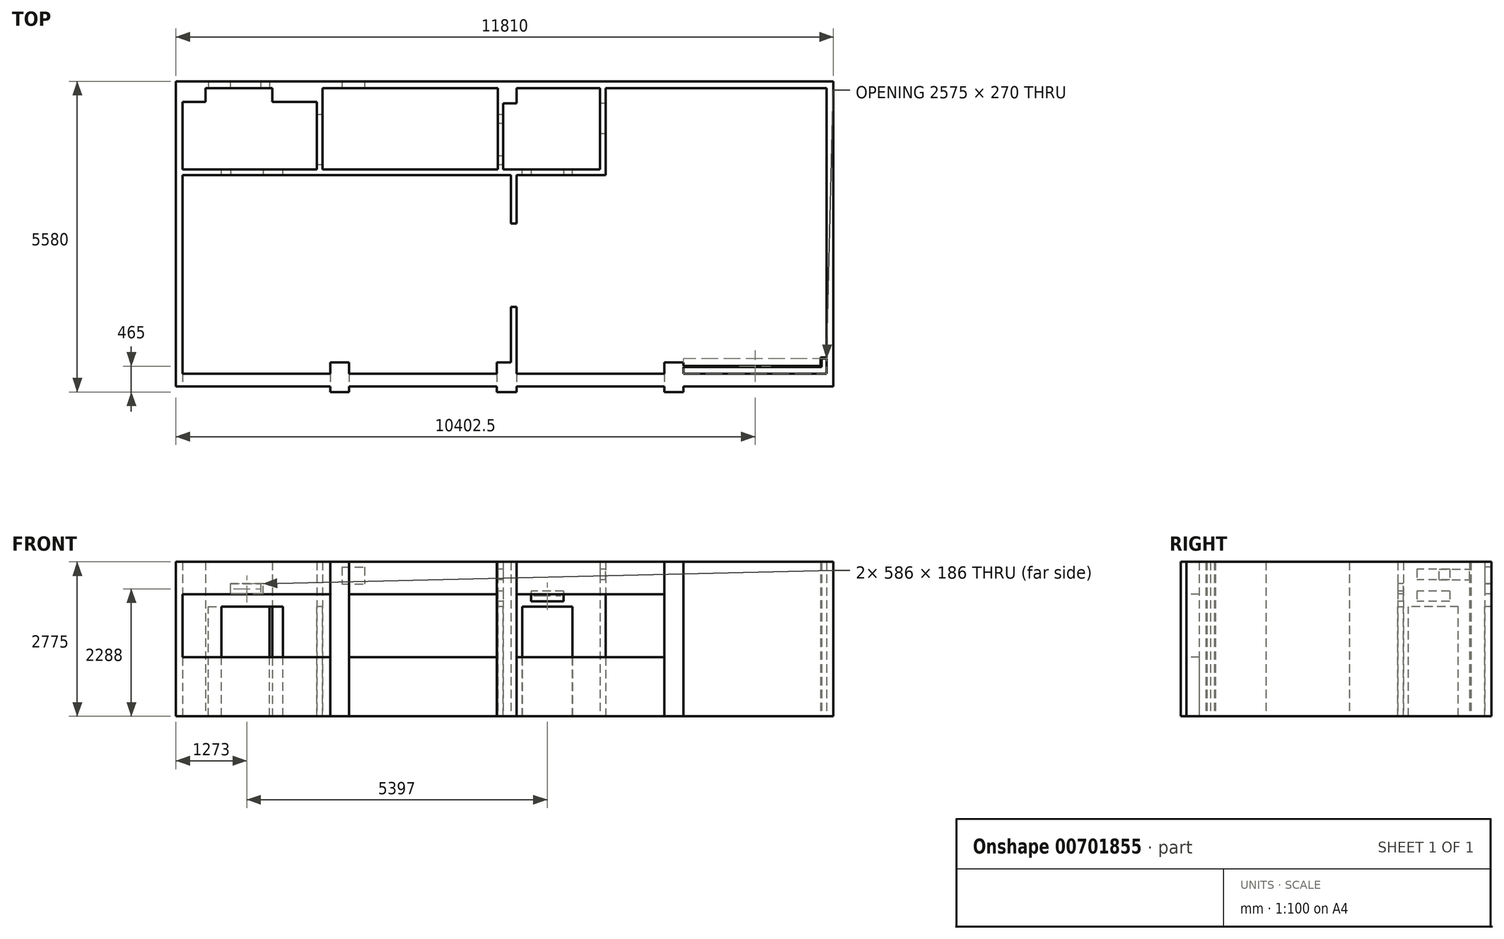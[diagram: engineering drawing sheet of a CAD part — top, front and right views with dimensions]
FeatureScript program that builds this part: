
annotation { "Feature Type Name" : "Feature", "Feature Type Description" : "" }
export const myFeature = defineFeature(function(context is Context, id is Id, definition is map)
    precondition{}
    {
        {
            var Q0;
            Q0=qCreatedBy(makeId("Top.planeOp"),FACE);
            var sketch = newSketch(context, id + "F0", { "sketchPlane" : qUnion([Q0])});
            skLineSegment(sketch, "E0.bottom", {"start": v(0, 0) * mm, "end": v(-5570, 0) * mm});
            skLineSegment(sketch, "E0.top", {"start": v(0, -5240) * mm, "end": v(-2575, -5240) * mm, "construction": true});
            skLineSegment(sketch, "E0.left", {"start": v(0, 0) * mm, "end": v(0, -5240) * mm});
            skLineSegment(sketch, "E0.right", {"start": v(-11570, -250) * mm, "end": v(-11570, -5130) * mm});
            skLineSegment(sketch, "E1.bottom", {"start": v(-11690, 120) * mm, "end": v(120, 120) * mm});
            skLineSegment(sketch, "E1.top", {"start": v(-11690, -5360) * mm, "end": v(-8920, -5360) * mm});
            skLineSegment(sketch, "E1.left", {"start": v(-11690, 120) * mm, "end": v(-11690, -5360) * mm});
            skLineSegment(sketch, "E1.right", {"start": v(120, 120) * mm, "end": v(120, -5360) * mm});
            skLineSegment(sketch, "E2.trimOffspring", {"start": v(-5925, -5240) * mm, "end": v(-8580, -5240) * mm, "construction": true});
            skLineSegment(sketch, "E3.trimOffspring", {"start": v(-5910, 0) * mm, "end": v(-9070, 0) * mm});
            skLineSegment(sketch, "E4", {"start": v(-5910, 0) * mm, "end": v(-5910, -275) * mm});
            skLineSegment(sketch, "E5", {"start": v(-5910, -275) * mm, "end": v(-5570, -275) * mm});
            skLineSegment(sketch, "E6", {"start": v(-5570, -275) * mm, "end": v(-5570, 0) * mm});
            skLineSegment(sketch, "E7", {"start": v(-5925, -5130) * mm, "end": v(-5925, -4930) * mm});
            skLineSegment(sketch, "E8", {"start": v(-5925, -4930) * mm, "end": v(-5570, -4930) * mm});
            skLineSegment(sketch, "E9", {"start": v(-5570, -4930) * mm, "end": v(-5570, -5130) * mm});
            skLineSegment(sketch, "E10.top", {"start": v(-8580, -4930) * mm, "end": v(-8920, -4930) * mm});
            skLineSegment(sketch, "E10.left", {"start": v(-8580, -5130) * mm, "end": v(-8580, -4930) * mm});
            skLineSegment(sketch, "E10.right", {"start": v(-8920, -5130) * mm, "end": v(-8920, -4930) * mm});
            skLineSegment(sketch, "E11.trimOffspring", {"start": v(-8920, -5240) * mm, "end": v(-11570, -5240) * mm, "construction": true});
            skLineSegment(sketch, "E12.top", {"start": v(-11570, -250) * mm, "end": v(-11160, -250) * mm});
            skLineSegment(sketch, "E12.right", {"start": v(-11160, 0) * mm, "end": v(-11160, -250) * mm});
            skLineSegment(sketch, "E13.top", {"start": v(-9960, -250) * mm, "end": v(-9070, -250) * mm});
            skLineSegment(sketch, "E13.left", {"start": v(-9960, 0) * mm, "end": v(-9960, -250) * mm});
            skLineSegment(sketch, "E13.right", {"start": v(-9070, 0) * mm, "end": v(-9070, -250) * mm});
            skLineSegment(sketch, "E14.trimOffspring", {"start": v(-9960, 0) * mm, "end": v(-11160, 0) * mm});
            skLineSegment(sketch, "E15.top", {"start": v(-2915, -4930) * mm, "end": v(-2575, -4930) * mm});
            skLineSegment(sketch, "E15.left", {"start": v(-2915, -5130) * mm, "end": v(-2915, -4930) * mm});
            skLineSegment(sketch, "E15.right", {"start": v(-2575, -5130) * mm, "end": v(-2575, -4930) * mm});
            skLineSegment(sketch, "E16.top", {"start": v(-2575, -5460) * mm, "end": v(-2915, -5460) * mm});
            skLineSegment(sketch, "E16.left", {"start": v(-2575, -5360) * mm, "end": v(-2575, -5460) * mm});
            skLineSegment(sketch, "E16.right", {"start": v(-2915, -5360) * mm, "end": v(-2915, -5460) * mm});
            skLineSegment(sketch, "E17.trimOffspring", {"start": v(-2575, -5360) * mm, "end": v(120, -5360) * mm});
            skLineSegment(sketch, "E18.trimOffspring", {"start": v(-2915, -5240) * mm, "end": v(-5570, -5240) * mm, "construction": true});
            skLineSegment(sketch, "E19.top", {"start": v(-5570, -5460) * mm, "end": v(-5925, -5460) * mm});
            skLineSegment(sketch, "E19.left", {"start": v(-5570, -5360) * mm, "end": v(-5570, -5460) * mm});
            skLineSegment(sketch, "E19.right", {"start": v(-5925, -5360) * mm, "end": v(-5925, -5460) * mm});
            skLineSegment(sketch, "E20.top", {"start": v(-8580, -5460) * mm, "end": v(-8920, -5460) * mm});
            skLineSegment(sketch, "E20.left", {"start": v(-8580, -5360) * mm, "end": v(-8580, -5460) * mm});
            skLineSegment(sketch, "E20.right", {"start": v(-8920, -5360) * mm, "end": v(-8920, -5460) * mm});
            skLineSegment(sketch, "E21.trimOffspring", {"start": v(-8580, -5360) * mm, "end": v(-5925, -5360) * mm});
            skLineSegment(sketch, "E22.trimOffspring", {"start": v(-5570, -5360) * mm, "end": v(-2915, -5360) * mm});
            skLineSegment(sketch, "E23", {"start": v(-11570, -5130) * mm, "end": v(-8920, -5130) * mm});
            skLineSegment(sketch, "E24.trimOffspring", {"start": v(-8580, -5130) * mm, "end": v(-5925, -5130) * mm});
            skLineSegment(sketch, "E25.trimOffspring", {"start": v(-5570, -5130) * mm, "end": v(-2915, -5130) * mm});
            skLineSegment(sketch, "E26.trimOffspring", {"start": v(-2575, -5130) * mm, "end": v(0, -5130) * mm});
            skSolve(sketch);
        }
        {
            var Q0;
            Q0 = qSketchRegion(id + "F0", true);
            extrude(context, id + "F1", {"entities" : qUnion([Q0]), "depth" : 2775 * mm, "offsetDistance" : 25 * mm});
        }
        {
            var Q0;
            Q0=makeQuery(id+"F1.opExtrude","SWEPT_FACE",FACE,{"disambiguationData":[OSD([sQuery(id+"F0.wireOp",EDGE,"E0.bottom")])]});
            var sketch = newSketch(context, id + "F2", { "sketchPlane" : qUnion([Q0])});
            skLineSegment(sketch, "E27.bottom", {"start": v(-11110, 0) * mm, "end": v(-10010, 0) * mm});
            skLineSegment(sketch, "E27.top", {"start": v(-11110, 1970) * mm, "end": v(-10010, 1970) * mm});
            skLineSegment(sketch, "E27.left", {"start": v(-11110, 0) * mm, "end": v(-11110, 1970) * mm});
            skLineSegment(sketch, "E27.right", {"start": v(-10010, 0) * mm, "end": v(-10010, 1970) * mm});
            skSolve(sketch);
        }
        {
            var Q0;
            Q0 = qSketchRegion(id + "F2", true);
            extrude(context, id + "F3", {"entities" : qUnion([Q0]), "operationType" : NewBodyOperationType.REMOVE, "endBound" : BoundingType.UP_TO_NEXT, "oppositeDirection" : true, "depth" : 25 * mm, "offsetDistance" : 25 * mm});
        }
        {
            var Q0;
            Q0=qCreatedBy(makeId("Top.planeOp"),FACE);
            var sketch = newSketch(context, id + "F4", { "sketchPlane" : qUnion([Q0])});
            skLineSegment(sketch, "E28.top", {"start": v(-5670, -4930) * mm, "end": v(-5570, -4930) * mm});
            skLineSegment(sketch, "E28.left", {"start": v(-5670, -1460) * mm, "end": v(-5670, -4930) * mm});
            skLineSegment(sketch, "E28.right", {"start": v(-5570, -1460) * mm, "end": v(-5570, -4930) * mm});
            skLineSegment(sketch, "E29", {"start": v(-5570, -1460) * mm, "end": v(-5670, -1460) * mm});
            skLineSegment(sketch, "E30", {"start": v(-5670, -2430) * mm, "end": v(-5570, -2430) * mm});
            skLineSegment(sketch, "E31", {"start": v(-5670, -3930) * mm, "end": v(-5570, -3930) * mm});
            skSolve(sketch);
        }
        {
            var Q0;
            {var subQ0=sQuery(id+"F4.wireOp",EDGE,"E28.top");Q0=makeQuery(id+"F4.imprint","IMPRINT",FACE,{"disambiguationData":[TD([[makeQuery(id+"F4.imprint","IMPRINT",EDGE,{"derivedFrom":subQ0}),1.0]])]});}
            var Q1;
            {var subQ0=sQuery(id+"F4.wireOp",EDGE,"E29");Q1=makeQuery(id+"F4.imprint","IMPRINT",FACE,{"disambiguationData":[TD([[makeQuery(id+"F4.imprint","IMPRINT",EDGE,{"derivedFrom":subQ0}),1.0]])]});}
            var Q2;
            Q2=makeQuery(id+"F1.opExtrude","CAP_FACE",FACE,{"disambiguationData":[OSD([sQuery(id+"F0.wireOp",EDGE,"E0.bottom"),sQuery(id+"F0.wireOp",EDGE,"E0.top"),sQuery(id+"F0.wireOp",EDGE,"E0.left"),sQuery(id+"F0.wireOp",EDGE,"E0.right"),sQuery(id+"F0.wireOp",EDGE,"E1.bottom"),sQuery(id+"F0.wireOp",EDGE,"E1.top"),sQuery(id+"F0.wireOp",EDGE,"E1.left"),sQuery(id+"F0.wireOp",EDGE,"E1.right")])],"isStart":false});
            extrude(context, id + "F5", {"entities" : qUnion([Q0, Q1]), "operationType" : NewBodyOperationType.ADD, "endBound" : BoundingType.UP_TO_SURFACE, "depth" : 25 * mm, "endBoundEntityFace" : qUnion([Q2]), "offsetDistance" : 25 * mm});
        }
        {
            var Q0;
            Q0=qCreatedBy(makeId("Top.planeOp"),FACE);
            var sketch = newSketch(context, id + "F6", { "sketchPlane" : qUnion([Q0])});
            skLineSegment(sketch, "E32.bottom", {"start": v(-5670, -1460) * mm, "end": v(-11570, -1460) * mm});
            skLineSegment(sketch, "E32.top", {"start": v(-5670, -1560) * mm, "end": v(-11570, -1560) * mm});
            skLineSegment(sketch, "E32.left", {"start": v(-5670, -1460) * mm, "end": v(-5670, -1560) * mm});
            skLineSegment(sketch, "E32.right", {"start": v(-11570, -1460) * mm, "end": v(-11570, -1560) * mm});
            skSolve(sketch);
        }
        {
            var Q0;
            Q0=makeQuery(id+"F6.imprint","IMPRINT",FACE,{"disambiguationData":[TD([[makeQuery(id+"F6.imprint","IMPRINT",EDGE,{"derivedFrom":sQuery(id+"F6.wireOp",EDGE,"E32.bottom")}),1.0]])]});
            var Q1;
            {var subQ0=sQuery(id+"F0.wireOp",EDGE,"E1.right");var subQ1=sQuery(id+"F0.wireOp",EDGE,"E1.left");var subQ2=sQuery(id+"F0.wireOp",EDGE,"E1.top");var subQ3=sQuery(id+"F0.wireOp",EDGE,"E1.bottom");var subQ4=sQuery(id+"F0.wireOp",EDGE,"E0.right");var subQ5=sQuery(id+"F0.wireOp",EDGE,"E0.left");var subQ6=sQuery(id+"F0.wireOp",EDGE,"E0.top");var subQ7=sQuery(id+"F0.wireOp",EDGE,"E0.bottom");Q1=makeQuery(id+"F5.boolean.opBoolean","MERGE",FACE,{"derivedFrom":[makeQuery(id+"F1.opExtrude","CAP_FACE",FACE,{"disambiguationData":[OSD([subQ7,subQ6,subQ5,subQ4,subQ3,subQ2,subQ1,subQ0])],"isStart":false}),makeQuery(id+"F5.opExtrude","CAP_FACE",FACE,{"disambiguationData":[OSD([subQ7,subQ6,subQ5,subQ4,subQ3,subQ2,subQ1,subQ0])],"isStart":false})]});}
            extrude(context, id + "F7", {"entities" : qUnion([Q0]), "operationType" : NewBodyOperationType.ADD, "endBound" : BoundingType.UP_TO_SURFACE, "depth" : 25 * mm, "endBoundEntityFace" : qUnion([Q1]), "offsetDistance" : 25 * mm});
        }
        {
            var Q0;
            Q0=qCreatedBy(makeId("Top.planeOp"),FACE);
            var sketch = newSketch(context, id + "F8", { "sketchPlane" : qUnion([Q0])});
            skLineSegment(sketch, "E33.bottom", {"start": v(-9060, 0) * mm, "end": v(-9160, 0) * mm});
            skLineSegment(sketch, "E33.top", {"start": v(-9060, -1460) * mm, "end": v(-9160, -1460) * mm});
            skLineSegment(sketch, "E33.left", {"start": v(-9060, 0) * mm, "end": v(-9060, -1460) * mm});
            skLineSegment(sketch, "E33.right", {"start": v(-9160, 0) * mm, "end": v(-9160, -1460) * mm});
            skSolve(sketch);
        }
        {
            var Q0;
            Q0=makeQuery(id+"F8.imprint","IMPRINT",FACE,{"disambiguationData":[TD([[makeQuery(id+"F8.imprint","IMPRINT",EDGE,{"derivedFrom":sQuery(id+"F8.wireOp",EDGE,"E33.bottom")}),1.0]])]});
            var Q1;
            {var subQ0=sQuery(id+"F0.wireOp",EDGE,"E1.right");var subQ1=sQuery(id+"F0.wireOp",EDGE,"E1.left");var subQ2=sQuery(id+"F0.wireOp",EDGE,"E1.top");var subQ3=sQuery(id+"F0.wireOp",EDGE,"E1.bottom");var subQ4=sQuery(id+"F0.wireOp",EDGE,"E0.right");var subQ5=sQuery(id+"F0.wireOp",EDGE,"E0.left");var subQ6=sQuery(id+"F0.wireOp",EDGE,"E0.top");var subQ7=sQuery(id+"F0.wireOp",EDGE,"E0.bottom");Q1=makeQuery(id+"F7.boolean.opBoolean","MERGE",FACE,{"derivedFrom":[makeQuery(id+"F5.boolean.opBoolean","MERGE",FACE,{"derivedFrom":[makeQuery(id+"F1.opExtrude","CAP_FACE",FACE,{"disambiguationData":[OSD([subQ7,subQ6,subQ5,subQ4,subQ3,subQ2,subQ1,subQ0])],"isStart":false}),makeQuery(id+"F5.opExtrude","CAP_FACE",FACE,{"disambiguationData":[OSD([subQ7,subQ6,subQ5,subQ4,subQ3,subQ2,subQ1,subQ0])],"isStart":false})]}),makeQuery(id+"F7.opExtrude","CAP_FACE",FACE,{"disambiguationData":[OSD([subQ7,subQ6,subQ5,subQ4,subQ3,subQ2,subQ1,subQ0])],"isStart":false})]});}
            extrude(context, id + "F9", {"entities" : qUnion([Q0]), "operationType" : NewBodyOperationType.ADD, "endBound" : BoundingType.UP_TO_SURFACE, "depth" : 25 * mm, "endBoundEntityFace" : qUnion([Q1]), "offsetDistance" : 25 * mm});
        }
        {
            var Q0;
            {var subQ0=sQuery(id+"F0.wireOp",EDGE,"E0.right");var subQ8=sQuery(id+"F6.wireOp",EDGE,"E32.bottom");Q0=makeQuery(id+"F9.boolean.opBoolean","SPLIT",FACE,{"disambiguationData":[TD([makeQuery(id+"F1.opExtrude","SWEPT_FACE",FACE,{"disambiguationData":[OSD([subQ0])]})])],"derivedFrom":makeQuery(id+"F7.opExtrude","SWEPT_FACE",FACE,{"disambiguationData":[OSD([subQ8])]})});}
            var sketch = newSketch(context, id + "F10", { "sketchPlane" : qUnion([Q0])});
            skLineSegment(sketch, "E34.bottom", {"start": v(9770, 0) * mm, "end": v(10870, 0) * mm});
            skLineSegment(sketch, "E34.top", {"start": v(9770, 1970) * mm, "end": v(10870, 1970) * mm});
            skLineSegment(sketch, "E34.left", {"start": v(9770, 0) * mm, "end": v(9770, 1970) * mm});
            skLineSegment(sketch, "E34.right", {"start": v(10870, 0) * mm, "end": v(10870, 1970) * mm});
            skSolve(sketch);
        }
        {
            var Q0;
            Q0=makeQuery(id+"F10.imprint","IMPRINT",FACE,{"disambiguationData":[TD([[makeQuery(id+"F10.imprint","IMPRINT",EDGE,{"derivedFrom":sQuery(id+"F10.wireOp",EDGE,"E34.bottom")}),1.0]])]});
            extrude(context, id + "F11", {"entities" : qUnion([Q0]), "operationType" : NewBodyOperationType.REMOVE, "endBound" : BoundingType.UP_TO_NEXT, "oppositeDirection" : true, "depth" : 25 * mm, "offsetDistance" : 25 * mm});
        }
        {
            var Q0;
            Q0=makeQuery(id+"F9.opExtrude","SWEPT_FACE",FACE,{"disambiguationData":[OSD([sQuery(id+"F8.wireOp",EDGE,"E33.right")])]});
            var sketch = newSketch(context, id + "F12", { "sketchPlane" : qUnion([Q0])});
            skLineSegment(sketch, "E35.bottom", {"start": v(475, 0) * mm, "end": v(1375, 0) * mm});
            skLineSegment(sketch, "E35.top", {"start": v(475, 1970) * mm, "end": v(1375, 1970) * mm});
            skLineSegment(sketch, "E35.left", {"start": v(475, 0) * mm, "end": v(475, 1970) * mm});
            skLineSegment(sketch, "E35.right", {"start": v(1375, 0) * mm, "end": v(1375, 1970) * mm});
            skPoint(sketch, "E36.startSnap0", {"position": v(925, 1970) * mm});
            skSolve(sketch);
        }
        {
            var Q0;
            Q0 = qSketchRegion(id + "F12", true);
            extrude(context, id + "F13", {"entities" : qUnion([Q0]), "operationType" : NewBodyOperationType.REMOVE, "endBound" : BoundingType.UP_TO_NEXT, "oppositeDirection" : true, "depth" : 25 * mm, "offsetDistance" : 25 * mm});
        }
        {
            var Q0;
            Q0=qCreatedBy(makeId("Top.planeOp"),FACE);
            var sketch = newSketch(context, id + "F14", { "sketchPlane" : qUnion([Q0])});
            skLineSegment(sketch, "E37.bottom", {"start": v(-5910, -275) * mm, "end": v(-5810, -275) * mm});
            skLineSegment(sketch, "E37.top", {"start": v(-5910, -1460) * mm, "end": v(-5810, -1460) * mm});
            skLineSegment(sketch, "E37.left", {"start": v(-5910, -275) * mm, "end": v(-5910, -1460) * mm});
            skLineSegment(sketch, "E37.right", {"start": v(-5810, -275) * mm, "end": v(-5810, -1460) * mm});
            skSolve(sketch);
        }
        {
            var Q0;
            Q0 = qSketchRegion(id + "F14", true);
            var Q1;
            {var subQ0=sQuery(id+"F0.wireOp",EDGE,"E3.trimOffspring");var subQ1=sQuery(id+"F0.wireOp",EDGE,"E2.trimOffspring");var subQ2=sQuery(id+"F0.wireOp",EDGE,"dA5mFhwm-C5pU-s43x-tqTS-3jepumlIrKXL.right");var subQ3=sQuery(id+"F0.wireOp",EDGE,"dA5mFhwm-C5pU-s43x-tqTS-3jepumlIrKXL.left");var subQ4=sQuery(id+"F0.wireOp",EDGE,"dA5mFhwm-C5pU-s43x-tqTS-3jepumlIrKXL.top");var subQ5=sQuery(id+"F0.wireOp",EDGE,"zGKuHS85-YCsc-AVKT-CzAw-lwCyFNVVRMQ6.right");var subQ6=sQuery(id+"F0.wireOp",EDGE,"zGKuHS85-YCsc-AVKT-CzAw-lwCyFNVVRMQ6.left");var subQ7=sQuery(id+"F0.wireOp",EDGE,"zGKuHS85-YCsc-AVKT-CzAw-lwCyFNVVRMQ6.top");var subQ8=sQuery(id+"F0.wireOp",EDGE,"E1.right");var subQ9=sQuery(id+"F0.wireOp",EDGE,"E1.left");var subQ10=sQuery(id+"F0.wireOp",EDGE,"E1.top");var subQ11=sQuery(id+"F0.wireOp",EDGE,"E1.bottom");var subQ12=sQuery(id+"F0.wireOp",EDGE,"E0.right");var subQ13=sQuery(id+"F0.wireOp",EDGE,"E0.left");var subQ14=sQuery(id+"F0.wireOp",EDGE,"E0.top");var subQ15=sQuery(id+"F0.wireOp",EDGE,"E0.bottom");Q1=makeQuery(id+"F9.boolean.opBoolean","MERGE",FACE,{"derivedFrom":[makeQuery(id+"F7.boolean.opBoolean","MERGE",FACE,{"derivedFrom":[makeQuery(id+"F5.boolean.opBoolean","MERGE",FACE,{"derivedFrom":[makeQuery(id+"F1.opExtrude","CAP_FACE",FACE,{"disambiguationData":[OSD([subQ15,subQ14,subQ13,subQ12,subQ11,subQ10,subQ9,subQ8,subQ7,subQ6,subQ5,subQ4,subQ3,subQ2,subQ1,subQ0])],"isStart":false}),makeQuery(id+"F5.opExtrude","CAP_FACE",FACE,{"disambiguationData":[OSD([subQ15,subQ14,subQ13,subQ12,subQ11,subQ10,subQ9,subQ8,subQ7,subQ6,subQ5,subQ4,subQ3,subQ2,subQ1,subQ0])],"isStart":false})]}),makeQuery(id+"F7.opExtrude","CAP_FACE",FACE,{"disambiguationData":[OSD([subQ15,subQ14,subQ13,subQ12,subQ11,subQ10,subQ9,subQ8,subQ7,subQ6,subQ5,subQ4,subQ3,subQ2,subQ1,subQ0])],"isStart":false})]}),makeQuery(id+"F9.opExtrude","CAP_FACE",FACE,{"disambiguationData":[OSD([subQ15,subQ14,subQ13,subQ12,subQ11,subQ10,subQ9,subQ8,subQ7,subQ6,subQ5,subQ4,subQ3,subQ2,subQ1,subQ0])],"isStart":false})]});}
            extrude(context, id + "F15", {"entities" : qUnion([Q0]), "operationType" : NewBodyOperationType.ADD, "endBound" : BoundingType.UP_TO_SURFACE, "depth" : 25 * mm, "endBoundEntityFace" : qUnion([Q1]), "offsetDistance" : 25 * mm});
        }
        {
            var Q0;
            Q0=makeQuery(id+"F15.boolean.opBoolean","MERGE",FACE,{"derivedFrom":[makeQuery(id+"F1.opExtrude","SWEPT_FACE",FACE,{"disambiguationData":[OSD([sQuery(id+"F0.wireOp",EDGE,"zGKuHS85-YCsc-AVKT-CzAw-lwCyFNVVRMQ6.right")])]}),makeQuery(id+"F15.opExtrude","SWEPT_FACE",FACE,{"disambiguationData":[OSD([sQuery(id+"F14.wireOp",EDGE,"E37.left")])]})]});
            var sketch = newSketch(context, id + "F16", { "sketchPlane" : qUnion([Q0])});
            skLineSegment(sketch, "E38.bottom", {"start": v(475, 0) * mm, "end": v(1375, 0) * mm});
            skLineSegment(sketch, "E38.top", {"start": v(475, 1970) * mm, "end": v(1375, 1970) * mm});
            skLineSegment(sketch, "E38.left", {"start": v(475, 0) * mm, "end": v(475, 1970) * mm});
            skLineSegment(sketch, "E38.right", {"start": v(1375, 0) * mm, "end": v(1375, 1970) * mm});
            skSolve(sketch);
        }
        {
            var Q0;
            Q0 = qSketchRegion(id + "F16", true);
            var Q1;
            Q1=makeQuery(id+"F15.opExtrude","SWEPT_FACE",FACE,{"disambiguationData":[OSD([sQuery(id+"F14.wireOp",EDGE,"E37.right")])]});
            extrude(context, id + "F17", {"entities" : qUnion([Q0]), "operationType" : NewBodyOperationType.REMOVE, "endBound" : BoundingType.UP_TO_SURFACE, "oppositeDirection" : true, "depth" : 25 * mm, "endBoundEntityFace" : qUnion([Q1]), "offsetDistance" : 25 * mm});
        }
        {
            var Q0;
            Q0=qCreatedBy(makeId("Top.planeOp"),FACE);
            var sketch = newSketch(context, id + "F18", { "sketchPlane" : qUnion([Q0])});
            skLineSegment(sketch, "E39", {"start": v(-5570, -1560) * mm, "end": v(-3970, -1560) * mm});
            skLineSegment(sketch, "E40", {"start": v(-3970, -1560) * mm, "end": v(-3970, 0) * mm});
            skLineSegment(sketch, "E41", {"start": v(-3970, 0) * mm, "end": v(-4070, 0) * mm});
            skLineSegment(sketch, "E42", {"start": v(-4070, 0) * mm, "end": v(-4070, -1460) * mm});
            skLineSegment(sketch, "E43", {"start": v(-4070, -1460) * mm, "end": v(-5570, -1460) * mm});
            skLineSegment(sketch, "E44", {"start": v(-5570, -1460) * mm, "end": v(-5570, -1560) * mm});
            skSolve(sketch);
        }
        {
            var Q0;
            Q0=makeQuery(id+"F18.imprint","IMPRINT",FACE,{"disambiguationData":[TD([[makeQuery(id+"F18.imprint","IMPRINT",EDGE,{"derivedFrom":sQuery(id+"F18.wireOp",EDGE,"E39")}),1.0]])]});
            var Q1;
            {var subQ0=sQuery(id+"F0.wireOp",EDGE,"E3.trimOffspring");var subQ1=sQuery(id+"F0.wireOp",EDGE,"E2.trimOffspring");var subQ2=sQuery(id+"F0.wireOp",EDGE,"dA5mFhwm-C5pU-s43x-tqTS-3jepumlIrKXL.right");var subQ3=sQuery(id+"F0.wireOp",EDGE,"dA5mFhwm-C5pU-s43x-tqTS-3jepumlIrKXL.left");var subQ4=sQuery(id+"F0.wireOp",EDGE,"dA5mFhwm-C5pU-s43x-tqTS-3jepumlIrKXL.top");var subQ5=sQuery(id+"F0.wireOp",EDGE,"zGKuHS85-YCsc-AVKT-CzAw-lwCyFNVVRMQ6.right");var subQ6=sQuery(id+"F0.wireOp",EDGE,"zGKuHS85-YCsc-AVKT-CzAw-lwCyFNVVRMQ6.left");var subQ7=sQuery(id+"F0.wireOp",EDGE,"zGKuHS85-YCsc-AVKT-CzAw-lwCyFNVVRMQ6.top");var subQ8=sQuery(id+"F0.wireOp",EDGE,"E1.right");var subQ9=sQuery(id+"F0.wireOp",EDGE,"E1.left");var subQ10=sQuery(id+"F0.wireOp",EDGE,"E1.top");var subQ11=sQuery(id+"F0.wireOp",EDGE,"E1.bottom");var subQ12=sQuery(id+"F0.wireOp",EDGE,"E0.right");var subQ13=sQuery(id+"F0.wireOp",EDGE,"E0.left");var subQ14=sQuery(id+"F0.wireOp",EDGE,"E0.top");var subQ15=sQuery(id+"F0.wireOp",EDGE,"E0.bottom");Q1=makeQuery(id+"F15.boolean.opBoolean","MERGE",FACE,{"derivedFrom":[makeQuery(id+"F9.boolean.opBoolean","MERGE",FACE,{"derivedFrom":[makeQuery(id+"F7.boolean.opBoolean","MERGE",FACE,{"derivedFrom":[makeQuery(id+"F5.boolean.opBoolean","MERGE",FACE,{"derivedFrom":[makeQuery(id+"F1.opExtrude","CAP_FACE",FACE,{"disambiguationData":[OSD([subQ15,subQ14,subQ13,subQ12,subQ11,subQ10,subQ9,subQ8,subQ7,subQ6,subQ5,subQ4,subQ3,subQ2,subQ1,subQ0])],"isStart":false}),makeQuery(id+"F5.opExtrude","CAP_FACE",FACE,{"disambiguationData":[OSD([subQ15,subQ14,subQ13,subQ12,subQ11,subQ10,subQ9,subQ8,subQ7,subQ6,subQ5,subQ4,subQ3,subQ2,subQ1,subQ0])],"isStart":false})]}),makeQuery(id+"F7.opExtrude","CAP_FACE",FACE,{"disambiguationData":[OSD([subQ15,subQ14,subQ13,subQ12,subQ11,subQ10,subQ9,subQ8,subQ7,subQ6,subQ5,subQ4,subQ3,subQ2,subQ1,subQ0])],"isStart":false})]}),makeQuery(id+"F9.opExtrude","CAP_FACE",FACE,{"disambiguationData":[OSD([subQ15,subQ14,subQ13,subQ12,subQ11,subQ10,subQ9,subQ8,subQ7,subQ6,subQ5,subQ4,subQ3,subQ2,subQ1,subQ0])],"isStart":false})]}),makeQuery(id+"F15.opExtrude","CAP_FACE",FACE,{"disambiguationData":[OSD([subQ15,subQ14,subQ13,subQ12,subQ11,subQ10,subQ9,subQ8,subQ7,subQ6,subQ5,subQ4,subQ3,subQ2,subQ1,subQ0])],"isStart":false})]});}
            extrude(context, id + "F19", {"entities" : qUnion([Q0]), "operationType" : NewBodyOperationType.ADD, "endBound" : BoundingType.UP_TO_SURFACE, "depth" : 25 * mm, "endBoundEntityFace" : qUnion([Q1]), "offsetDistance" : 25 * mm});
        }
        {
            var Q0;
            Q0=makeQuery(id+"F19.opExtrude","SWEPT_FACE",FACE,{"disambiguationData":[OSD([sQuery(id+"F18.wireOp",EDGE,"E43")])]});
            var sketch = newSketch(context, id + "F20", { "sketchPlane" : qUnion([Q0])});
            skLineSegment(sketch, "E45.bottom", {"start": v(4570, 0) * mm, "end": v(5470, 0) * mm});
            skLineSegment(sketch, "E45.top", {"start": v(4570, 1970) * mm, "end": v(5470, 1970) * mm});
            skLineSegment(sketch, "E45.left", {"start": v(4570, 0) * mm, "end": v(4570, 1970) * mm});
            skLineSegment(sketch, "E45.right", {"start": v(5470, 0) * mm, "end": v(5470, 1970) * mm});
            skSolve(sketch);
        }
        {
            var Q0;
            Q0=makeQuery(id+"F20.imprint","IMPRINT",FACE,{"disambiguationData":[TD([[makeQuery(id+"F20.imprint","IMPRINT",EDGE,{"derivedFrom":sQuery(id+"F20.wireOp",EDGE,"E45.bottom")}),1.0]])]});
            extrude(context, id + "F21", {"entities" : qUnion([Q0]), "operationType" : NewBodyOperationType.REMOVE, "endBound" : BoundingType.UP_TO_NEXT, "oppositeDirection" : true, "depth" : 25 * mm, "offsetDistance" : 25 * mm});
        }
        {
            var Q0;
            Q0=makeQuery(id+"F1.opExtrude","SWEPT_FACE",FACE,{"disambiguationData":[OSD([sQuery(id+"F0.wireOp",EDGE,"E1.top")])]});
            var sketch = newSketch(context, id + "F22", { "sketchPlane" : qUnion([Q0])});
            skLineSegment(sketch, "E46.bottom", {"start": v(-2915, 2190) * mm, "end": v(-5570, 2190) * mm});
            skLineSegment(sketch, "E46.top", {"start": v(-2915, 1060) * mm, "end": v(-5570, 1060) * mm});
            skLineSegment(sketch, "E46.left", {"start": v(-2915, 2190) * mm, "end": v(-2915, 1060) * mm});
            skLineSegment(sketch, "E46.right", {"start": v(-5570, 2190) * mm, "end": v(-5570, 1060) * mm});
            skSolve(sketch);
        }
        {
            var Q0;
            Q0=makeQuery(id+"F22.imprint","IMPRINT",FACE,{"disambiguationData":[TD([[makeQuery(id+"F22.imprint","IMPRINT",EDGE,{"derivedFrom":sQuery(id+"F22.wireOp",EDGE,"UQFrSV9A-AeNk-hTGs-XUq7-kkI5QUDZIYbv.bottom")}),1.0]])]});
            var Q1;
            Q1=makeQuery(id+"F22.imprint","IMPRINT",FACE,{"disambiguationData":[TD([[makeQuery(id+"F22.imprint","IMPRINT",EDGE,{"derivedFrom":sQuery(id+"F22.wireOp",EDGE,"E46.bottom")}),1.0]])]});
            extrude(context, id + "F23", {"entities" : qUnion([Q0, Q1]), "operationType" : NewBodyOperationType.REMOVE, "endBound" : BoundingType.UP_TO_NEXT, "oppositeDirection" : true, "depth" : 25 * mm, "offsetDistance" : 25 * mm});
        }
        {
            var Q0;
            Q0=makeQuery(id+"F1.opExtrude","SWEPT_FACE",FACE,{"disambiguationData":[OSD([sQuery(id+"F0.wireOp",EDGE,"E1.top")])]});
            var sketch = newSketch(context, id + "F24", { "sketchPlane" : qUnion([Q0])});
            skLineSegment(sketch, "E47.bottom", {"start": v(-5925, 2190) * mm, "end": v(-8580, 2190) * mm});
            skLineSegment(sketch, "E47.top", {"start": v(-5925, 1060) * mm, "end": v(-8580, 1060) * mm});
            skLineSegment(sketch, "E47.left", {"start": v(-5925, 2190) * mm, "end": v(-5925, 1060) * mm});
            skLineSegment(sketch, "E47.right", {"start": v(-8580, 2190) * mm, "end": v(-8580, 1060) * mm});
            skLineSegment(sketch, "E48.bottom", {"start": v(-8920, 2190) * mm, "end": v(-11570, 2190) * mm});
            skLineSegment(sketch, "E48.top", {"start": v(-8920, 1060) * mm, "end": v(-11570, 1060) * mm});
            skLineSegment(sketch, "E48.left", {"start": v(-8920, 2190) * mm, "end": v(-8920, 1060) * mm});
            skLineSegment(sketch, "E48.right", {"start": v(-11570, 2190) * mm, "end": v(-11570, 1060) * mm});
            skSolve(sketch);
        }
        {
            var Q0;
            Q0=makeQuery(id+"F24.imprint","IMPRINT",FACE,{"disambiguationData":[TD([[makeQuery(id+"F24.imprint","IMPRINT",EDGE,{"derivedFrom":sQuery(id+"F24.wireOp",EDGE,"E48.bottom")}),1.0]])]});
            var Q1;
            Q1=makeQuery(id+"F24.imprint","IMPRINT",FACE,{"disambiguationData":[TD([[makeQuery(id+"F24.imprint","IMPRINT",EDGE,{"derivedFrom":sQuery(id+"F24.wireOp",EDGE,"E47.bottom")}),1.0]])]});
            extrude(context, id + "F25", {"entities" : qUnion([Q0, Q1]), "operationType" : NewBodyOperationType.REMOVE, "endBound" : BoundingType.UP_TO_NEXT, "oppositeDirection" : true, "depth" : 25 * mm, "offsetDistance" : 25 * mm});
        }
        {
            var Q0;
            Q0=makeQuery(id+"F1.opExtrude","SWEPT_FACE",FACE,{"disambiguationData":[OSD([sQuery(id+"F0.wireOp",EDGE,"E3.trimOffspring")])]});
            var sketch = newSketch(context, id + "F26", { "sketchPlane" : qUnion([Q0])});
            skLineSegment(sketch, "E49.bottom", {"start": v(-8710, 2680) * mm, "end": v(-8304, 2680) * mm});
            skLineSegment(sketch, "E49.top", {"start": v(-8710, 2374) * mm, "end": v(-8304, 2374) * mm});
            skLineSegment(sketch, "E49.left", {"start": v(-8710, 2680) * mm, "end": v(-8710, 2374) * mm});
            skLineSegment(sketch, "E49.right", {"start": v(-8304, 2680) * mm, "end": v(-8304, 2374) * mm});
            skSolve(sketch);
        }
        {
            var Q0;
            Q0=makeQuery(id+"F26.imprint","IMPRINT",FACE,{"disambiguationData":[TD([[makeQuery(id+"F26.imprint","IMPRINT",EDGE,{"derivedFrom":sQuery(id+"F26.wireOp",EDGE,"E49.bottom")}),-1.0]])]});
            extrude(context, id + "F27", {"entities" : qUnion([Q0]), "operationType" : NewBodyOperationType.REMOVE, "endBound" : BoundingType.UP_TO_NEXT, "oppositeDirection" : true, "depth" : 25 * mm, "offsetDistance" : 25 * mm});
        }
        {
            var Q0;
            Q0=makeQuery(id+"F19.opExtrude","SWEPT_FACE",FACE,{"disambiguationData":[OSD([sQuery(id+"F18.wireOp",EDGE,"E42")])]});
            var sketch = newSketch(context, id + "F28", { "sketchPlane" : qUnion([Q0])});
            skLineSegment(sketch, "E50.bottom", {"start": v(275, 2640) * mm, "end": v(821, 2640) * mm});
            skLineSegment(sketch, "E50.top", {"start": v(275, 2454) * mm, "end": v(821, 2454) * mm});
            skLineSegment(sketch, "E50.left", {"start": v(275, 2640) * mm, "end": v(275, 2454) * mm});
            skLineSegment(sketch, "E50.right", {"start": v(821, 2640) * mm, "end": v(821, 2454) * mm});
            skSolve(sketch);
        }
        {
            var Q0;
            Q0=makeQuery(id+"F28.imprint","IMPRINT",FACE,{"disambiguationData":[TD([[makeQuery(id+"F28.imprint","IMPRINT",EDGE,{"derivedFrom":sQuery(id+"F28.wireOp",EDGE,"E50.bottom")}),-1.0]])]});
            extrude(context, id + "F29", {"entities" : qUnion([Q0]), "operationType" : NewBodyOperationType.REMOVE, "endBound" : BoundingType.UP_TO_NEXT, "oppositeDirection" : true, "depth" : 25 * mm, "offsetDistance" : 25 * mm});
        }
        {
            var Q0;
            Q0=makeQuery(id+"F15.boolean.opBoolean","MERGE",FACE,{"derivedFrom":[makeQuery(id+"F1.opExtrude","SWEPT_FACE",FACE,{"disambiguationData":[OSD([sQuery(id+"F0.wireOp",EDGE,"E4")])]}),makeQuery(id+"F15.opExtrude","SWEPT_FACE",FACE,{"disambiguationData":[OSD([sQuery(id+"F14.wireOp",EDGE,"E37.left")])]})]});
            var sketch = newSketch(context, id + "F30", { "sketchPlane" : qUnion([Q0])});
            skLineSegment(sketch, "E51.bottom", {"start": v(632, 2640) * mm, "end": v(1218, 2640) * mm});
            skLineSegment(sketch, "E51.top", {"start": v(632, 2454) * mm, "end": v(1218, 2454) * mm});
            skLineSegment(sketch, "E51.left", {"start": v(632, 2640) * mm, "end": v(632, 2454) * mm});
            skLineSegment(sketch, "E51.right", {"start": v(1218, 2640) * mm, "end": v(1218, 2454) * mm});
            skLineSegment(sketch, "E52.bottom", {"start": v(632, 2251) * mm, "end": v(1218, 2251) * mm});
            skLineSegment(sketch, "E52.top", {"start": v(632, 2065) * mm, "end": v(1218, 2065) * mm});
            skLineSegment(sketch, "E52.left", {"start": v(632, 2251) * mm, "end": v(632, 2065) * mm});
            skLineSegment(sketch, "E52.right", {"start": v(1218, 2251) * mm, "end": v(1218, 2065) * mm});
            skSolve(sketch);
        }
        {
            var Q0;
            Q0=makeQuery(id+"F30.imprint","IMPRINT",FACE,{"disambiguationData":[TD([[makeQuery(id+"F30.imprint","IMPRINT",EDGE,{"derivedFrom":sQuery(id+"F30.wireOp",EDGE,"E51.bottom")}),-1.0]])]});
            var Q1;
            Q1=makeQuery(id+"F30.imprint","IMPRINT",FACE,{"disambiguationData":[TD([[makeQuery(id+"F30.imprint","IMPRINT",EDGE,{"derivedFrom":sQuery(id+"F30.wireOp",EDGE,"E52.bottom")}),-1.0]])]});
            extrude(context, id + "F31", {"entities" : qUnion([Q0, Q1]), "operationType" : NewBodyOperationType.REMOVE, "endBound" : BoundingType.UP_TO_NEXT, "oppositeDirection" : true, "depth" : 25 * mm, "offsetDistance" : 25 * mm});
        }
        {
            var Q0;
            Q0=makeQuery(id+"F1.opExtrude","SWEPT_FACE",FACE,{"disambiguationData":[OSD([sQuery(id+"F0.wireOp",EDGE,"E14.trimOffspring")])]});
            var sketch = newSketch(context, id + "F32", { "sketchPlane" : qUnion([Q0])});
            skLineSegment(sketch, "E53.bottom", {"start": v(-10716, 2381) * mm, "end": v(-10170, 2381) * mm});
            skLineSegment(sketch, "E53.top", {"start": v(-10716, 2195) * mm, "end": v(-10170, 2195) * mm});
            skLineSegment(sketch, "E53.left", {"start": v(-10716, 2381) * mm, "end": v(-10716, 2195) * mm});
            skLineSegment(sketch, "E53.right", {"start": v(-10170, 2381) * mm, "end": v(-10170, 2195) * mm});
            skSolve(sketch);
        }
        {
            var Q0;
            Q0=makeQuery(id+"F32.imprint","IMPRINT",FACE,{"disambiguationData":[TD([[makeQuery(id+"F32.imprint","IMPRINT",EDGE,{"derivedFrom":sQuery(id+"F32.wireOp",EDGE,"E53.bottom")}),-1.0]])]});
            extrude(context, id + "F33", {"entities" : qUnion([Q0]), "operationType" : NewBodyOperationType.REMOVE, "endBound" : BoundingType.UP_TO_NEXT, "oppositeDirection" : true, "depth" : 25 * mm, "offsetDistance" : 25 * mm});
        }
        {
            var Q0;
            Q0=makeQuery(id+"F7.opExtrude","SWEPT_FACE",FACE,{"disambiguationData":[OSD([sQuery(id+"F6.wireOp",EDGE,"E32.top")])]});
            var sketch = newSketch(context, id + "F34", { "sketchPlane" : qUnion([Q0])});
            skLineSegment(sketch, "E54.bottom", {"start": v(-10710, 2381) * mm, "end": v(-10124, 2381) * mm});
            skLineSegment(sketch, "E54.top", {"start": v(-10710, 2195) * mm, "end": v(-10124, 2195) * mm});
            skLineSegment(sketch, "E54.left", {"start": v(-10710, 2381) * mm, "end": v(-10710, 2195) * mm});
            skLineSegment(sketch, "E54.right", {"start": v(-10124, 2381) * mm, "end": v(-10124, 2195) * mm});
            skSolve(sketch);
        }
        {
            var Q0;
            Q0=makeQuery(id+"F34.imprint","IMPRINT",FACE,{"disambiguationData":[TD([[makeQuery(id+"F34.imprint","IMPRINT",EDGE,{"derivedFrom":sQuery(id+"F34.wireOp",EDGE,"E54.bottom")}),-1.0]])]});
            extrude(context, id + "F35", {"entities" : qUnion([Q0]), "operationType" : NewBodyOperationType.REMOVE, "endBound" : BoundingType.UP_TO_NEXT, "oppositeDirection" : true, "depth" : 25 * mm, "offsetDistance" : 25 * mm});
        }
        {
            var Q0;
            Q0=qCreatedBy(makeId("Top.planeOp"),FACE);
            var sketch = newSketch(context, id + "F36", { "sketchPlane" : qUnion([Q0])});
            skLineSegment(sketch, "E55.bottom", {"start": v(-2575, -4990) * mm, "end": v(-110, -4990) * mm});
            skLineSegment(sketch, "E55.top", {"start": v(-2575, -5010) * mm, "end": v(-90, -5010) * mm});
            skLineSegment(sketch, "E55.left", {"start": v(-2575, -4990) * mm, "end": v(-2575, -5010) * mm});
            skLineSegment(sketch, "E56.bottom", {"start": v(0, -4840) * mm, "end": v(-110, -4840) * mm});
            skLineSegment(sketch, "E56.left", {"start": v(0, -4840) * mm, "end": v(0, -4860) * mm});
            skLineSegment(sketch, "E56.right", {"start": v(-110, -4840) * mm, "end": v(-110, -4990) * mm});
            skLineSegment(sketch, "E57.0", {"start": v(-90, -4860) * mm, "end": v(-90, -5010) * mm});
            skLineSegment(sketch, "E57.1", {"start": v(0, -4860) * mm, "end": v(-90, -4860) * mm});
            skSolve(sketch);
        }
        {
            var Q0;
            Q0=makeQuery(id+"F36.imprint","IMPRINT",FACE,{"disambiguationData":[TD([[makeQuery(id+"F36.imprint","IMPRINT",EDGE,{"derivedFrom":sQuery(id+"F36.wireOp",EDGE,"E55.bottom")}),-1.0]])]});
            var Q1;
            {var subQ0=sQuery(id+"F0.wireOp",EDGE,"E26.trimOffspring");var subQ1=sQuery(id+"F0.wireOp",EDGE,"E25.trimOffspring");var subQ2=sQuery(id+"F0.wireOp",EDGE,"E24.trimOffspring");var subQ3=sQuery(id+"F0.wireOp",EDGE,"E23");var subQ4=sQuery(id+"F0.wireOp",EDGE,"E22.trimOffspring");var subQ5=sQuery(id+"F0.wireOp",EDGE,"E21.trimOffspring");var subQ6=sQuery(id+"F0.wireOp",EDGE,"E20.right");var subQ7=sQuery(id+"F0.wireOp",EDGE,"E20.left");var subQ8=sQuery(id+"F0.wireOp",EDGE,"E20.top");var subQ9=sQuery(id+"F0.wireOp",EDGE,"E19.right");var subQ10=sQuery(id+"F0.wireOp",EDGE,"E19.left");var subQ11=sQuery(id+"F0.wireOp",EDGE,"E19.top");var subQ12=sQuery(id+"F0.wireOp",EDGE,"E17.trimOffspring");var subQ13=sQuery(id+"F0.wireOp",EDGE,"E16.right");var subQ14=sQuery(id+"F0.wireOp",EDGE,"E16.left");var subQ15=sQuery(id+"F0.wireOp",EDGE,"E16.top");var subQ16=sQuery(id+"F0.wireOp",EDGE,"E15.right");var subQ17=sQuery(id+"F0.wireOp",EDGE,"E15.left");var subQ18=sQuery(id+"F0.wireOp",EDGE,"E15.top");var subQ19=sQuery(id+"F0.wireOp",EDGE,"E14.trimOffspring");var subQ20=sQuery(id+"F0.wireOp",EDGE,"E13.right");var subQ21=sQuery(id+"F0.wireOp",EDGE,"E13.left");var subQ22=sQuery(id+"F0.wireOp",EDGE,"E13.top");var subQ23=sQuery(id+"F0.wireOp",EDGE,"E12.right");var subQ24=sQuery(id+"F0.wireOp",EDGE,"E12.top");var subQ25=sQuery(id+"F0.wireOp",EDGE,"E10.right");var subQ26=sQuery(id+"F0.wireOp",EDGE,"E10.left");var subQ27=sQuery(id+"F0.wireOp",EDGE,"E10.top");var subQ28=sQuery(id+"F0.wireOp",EDGE,"E9");var subQ29=sQuery(id+"F0.wireOp",EDGE,"E8");var subQ30=sQuery(id+"F0.wireOp",EDGE,"E7");var subQ31=sQuery(id+"F0.wireOp",EDGE,"E6");var subQ32=sQuery(id+"F0.wireOp",EDGE,"E5");var subQ33=sQuery(id+"F0.wireOp",EDGE,"E4");var subQ34=sQuery(id+"F0.wireOp",EDGE,"E3.trimOffspring");var subQ35=sQuery(id+"F0.wireOp",EDGE,"E1.right");var subQ36=sQuery(id+"F0.wireOp",EDGE,"E1.left");var subQ37=sQuery(id+"F0.wireOp",EDGE,"E1.top");var subQ38=sQuery(id+"F0.wireOp",EDGE,"E1.bottom");var subQ39=sQuery(id+"F0.wireOp",EDGE,"E0.right");var subQ40=sQuery(id+"F0.wireOp",EDGE,"E0.left");var subQ41=sQuery(id+"F0.wireOp",EDGE,"E0.bottom");Q1=makeQuery(id+"F19.boolean.opBoolean","MERGE",FACE,{"derivedFrom":[makeQuery(id+"F15.boolean.opBoolean","MERGE",FACE,{"derivedFrom":[makeQuery(id+"F9.boolean.opBoolean","MERGE",FACE,{"derivedFrom":[makeQuery(id+"F7.boolean.opBoolean","MERGE",FACE,{"derivedFrom":[makeQuery(id+"F5.boolean.opBoolean","MERGE",FACE,{"derivedFrom":[makeQuery(id+"F1.opExtrude","CAP_FACE",FACE,{"disambiguationData":[OSD([subQ41,subQ40,subQ39,subQ38,subQ37,subQ36,subQ35,subQ34,subQ33,subQ32,subQ31,subQ30,subQ29,subQ28,subQ27,subQ26,subQ25,subQ24,subQ23,subQ22,subQ21,subQ20,subQ19,subQ18,subQ17,subQ16,subQ15,subQ14,subQ13,subQ12,subQ11,subQ10,subQ9,subQ8,subQ7,subQ6,subQ5,subQ4,subQ3,subQ2,subQ1,subQ0])],"isStart":false}),makeQuery(id+"F5.opExtrude","CAP_FACE",FACE,{"disambiguationData":[OSD([subQ41,subQ40,subQ39,subQ38,subQ37,subQ36,subQ35,subQ34,subQ33,subQ32,subQ31,subQ30,subQ29,subQ28,subQ27,subQ26,subQ25,subQ24,subQ23,subQ22,subQ21,subQ20,subQ19,subQ18,subQ17,subQ16,subQ15,subQ14,subQ13,subQ12,subQ11,subQ10,subQ9,subQ8,subQ7,subQ6,subQ5,subQ4,subQ3,subQ2,subQ1,subQ0])],"isStart":false})]}),makeQuery(id+"F7.opExtrude","CAP_FACE",FACE,{"disambiguationData":[OSD([subQ41,subQ40,subQ39,subQ38,subQ37,subQ36,subQ35,subQ34,subQ33,subQ32,subQ31,subQ30,subQ29,subQ28,subQ27,subQ26,subQ25,subQ24,subQ23,subQ22,subQ21,subQ20,subQ19,subQ18,subQ17,subQ16,subQ15,subQ14,subQ13,subQ12,subQ11,subQ10,subQ9,subQ8,subQ7,subQ6,subQ5,subQ4,subQ3,subQ2,subQ1,subQ0])],"isStart":false})]}),makeQuery(id+"F9.opExtrude","CAP_FACE",FACE,{"disambiguationData":[OSD([subQ41,subQ40,subQ39,subQ38,subQ37,subQ36,subQ35,subQ34,subQ33,subQ32,subQ31,subQ30,subQ29,subQ28,subQ27,subQ26,subQ25,subQ24,subQ23,subQ22,subQ21,subQ20,subQ19,subQ18,subQ17,subQ16,subQ15,subQ14,subQ13,subQ12,subQ11,subQ10,subQ9,subQ8,subQ7,subQ6,subQ5,subQ4,subQ3,subQ2,subQ1,subQ0])],"isStart":false})]}),makeQuery(id+"F15.opExtrude","CAP_FACE",FACE,{"disambiguationData":[OSD([subQ41,subQ40,subQ39,subQ38,subQ37,subQ36,subQ35,subQ34,subQ33,subQ32,subQ31,subQ30,subQ29,subQ28,subQ27,subQ26,subQ25,subQ24,subQ23,subQ22,subQ21,subQ20,subQ19,subQ18,subQ17,subQ16,subQ15,subQ14,subQ13,subQ12,subQ11,subQ10,subQ9,subQ8,subQ7,subQ6,subQ5,subQ4,subQ3,subQ2,subQ1,subQ0])],"isStart":false})]}),makeQuery(id+"F19.opExtrude","CAP_FACE",FACE,{"disambiguationData":[OSD([subQ41,subQ40,subQ39,subQ38,subQ37,subQ36,subQ35,subQ34,subQ33,subQ32,subQ31,subQ30,subQ29,subQ28,subQ27,subQ26,subQ25,subQ24,subQ23,subQ22,subQ21,subQ20,subQ19,subQ18,subQ17,subQ16,subQ15,subQ14,subQ13,subQ12,subQ11,subQ10,subQ9,subQ8,subQ7,subQ6,subQ5,subQ4,subQ3,subQ2,subQ1,subQ0])],"isStart":false})]});}
            extrude(context, id + "F37", {"entities" : qUnion([Q0]), "operationType" : NewBodyOperationType.ADD, "endBound" : BoundingType.UP_TO_SURFACE, "depth" : 25 * mm, "endBoundEntityFace" : qUnion([Q1]), "offsetDistance" : 25 * mm});
        }
        {
            var Q0;
            Q0=makeQuery(id+"F19.opExtrude","SWEPT_FACE",FACE,{"disambiguationData":[OSD([sQuery(id+"F18.wireOp",EDGE,"E39")])]});
            var sketch = newSketch(context, id + "F38", { "sketchPlane" : qUnion([Q0])});
            skLineSegment(sketch, "E58.bottom", {"start": v(-5313, 2251) * mm, "end": v(-4727, 2251) * mm});
            skLineSegment(sketch, "E58.top", {"start": v(-5313, 2065) * mm, "end": v(-4727, 2065) * mm});
            skLineSegment(sketch, "E58.left", {"start": v(-5313, 2251) * mm, "end": v(-5313, 2065) * mm});
            skLineSegment(sketch, "E58.right", {"start": v(-4727, 2251) * mm, "end": v(-4727, 2065) * mm});
            skSolve(sketch);
        }
        {
            var Q0;
            Q0=makeQuery(id+"F38.imprint","IMPRINT",FACE,{"disambiguationData":[TD([[makeQuery(id+"F38.imprint","IMPRINT",EDGE,{"derivedFrom":sQuery(id+"F38.wireOp",EDGE,"E58.bottom")}),-1.0]])]});
            extrude(context, id + "F39", {"entities" : qUnion([Q0]), "operationType" : NewBodyOperationType.REMOVE, "endBound" : BoundingType.UP_TO_NEXT, "oppositeDirection" : true, "depth" : 25 * mm, "offsetDistance" : 25 * mm});
        }
    });
